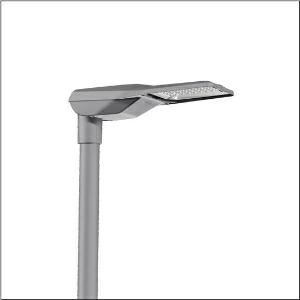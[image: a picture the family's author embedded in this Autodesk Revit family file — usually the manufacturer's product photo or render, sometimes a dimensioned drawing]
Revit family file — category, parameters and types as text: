
# Revit family: streetlight_sl_21_mini___st1_0a_5xe6d63a08hb_d3ee
name_source: partatom
category: Lighting Fixtures
units: mm (PartAtom-declared; Revit-internal decimal feet)

## family parameters
Cut with Voids When Loaded = No
Host = Face
Light Source = No
Part Type = Normal
Room Calculation Point = No
Round Connector Dimension = Use Diameter
Shared = No

## types (1)
- --- (1 x LED, 8110 lm, 66 W, 2700K)
    Apparent Load = 66 VA
    CIE Flux Codes = 37 72 97 100 100
    Color Rendering = 70
    Color Temperature = 2700K
    Default Elevation = 1800 mm
    Description = Streetlight SL 21 mini, mast luminaire, primary light control with lens, of PMMA, primary optical cover: cover, of toughened safety glass, transparent, light distribution: ST1.0a, light emission: direct distribution, primary light characteristic: asymmetric, installation type: post-top, side-entry, LED, 3G 1.5mm², High Power LED, rated luminous flux: 8.110lm, luminous efficacy: 123lm/W, light colour: 727, colour temperature: 2700K, control: overheat protection, constant luminous flux control, time-dependent luminous flux control, flexible luminous flux parameterisation, mains connection: 230..240V, AC, 50/60Hz, connection cable pre-assembled, cable length: 8,5m, wiring characteristics: H07RN-F, start of lifetime: 66W, end of service life: 69W, reduction: 30W, luminaire housing, of diecast aluminium, powder-coated, Siteco® metallic grey (DB 702S), corrosivity category C5 mid according to DIN EN ISO 12944, please order mast flange separately, inclination adjustable: 0°, 5°, 10°, 15°, sealing non-destructively replaceable, multi-level sealing system, length: 628mm, width: 235mm, height: 110mm, mast flange for spigot size: 42mm (side-entry): 5XC10008XM4, 60/48mm (side-entry/post-top): 5XC10108XM2, 76/60mm (side-entry/post-top): 5XC10108XM1, protection rating (complete): IP66, insulation class (complete): insulation class II (safety insulation), certification: CE, ENEC, ENEC+, VDE, impact resistance: IK09, permissible operating ambient temperature for outdoor applications: -40..+50°C, standard-compliant lighting for roads and squares, packaging unit: 1 piece

Light Distribution: ST1.0a
    Height = 110 mm
    Lamp = 1 x LED
    Lamp Light Flux = 8110 lm
    Lamp Power = 66 W
    Lamp count = 1
    Length = 625 mm
    Luminous efficacy = 123 lm/W
    Manufacturer = Siteco
    ModVariant = No
    Model = 5XE6D63A08HB
    Number of Poles = 1
    OnlyDefault = Yes
    Power Factor = 1
    Product Name = Streetlight SL 21 mini | ST1.0a
    Product group = mast luminaire | pylon top
    ProductGroupID = 6100
    Protection Class = Protection class II
    Protection Degree = IP 66
    RLX_Detail_Level = 1
    RLX_Emergency_Light_Flux = 0 lm
    RLX_Emergency_Type = 0
    RLX_Emergency_Type_DB = No
    RlxData = <blob elided: 92077 chars, md5=2508642e>
    Socket = socket
    Standby Power = 0 W
    System Light Flux = 8110 lm
    System Power = 66 W
    Type Comments = factory setting: luminous flux: 100 % | Output Level: 100 % | 670 mA
    Type Image = l_1003519.jpg
    URL = http://relux.com
    VarID = @adj_121901
    Voltage = 0 V
    Weight = 0.00 kg
    Width = 234 mm

## geometry (parser evidence)
native form markers: Blend x4, Sweep x11
no freeform markers — native parametric forms only
